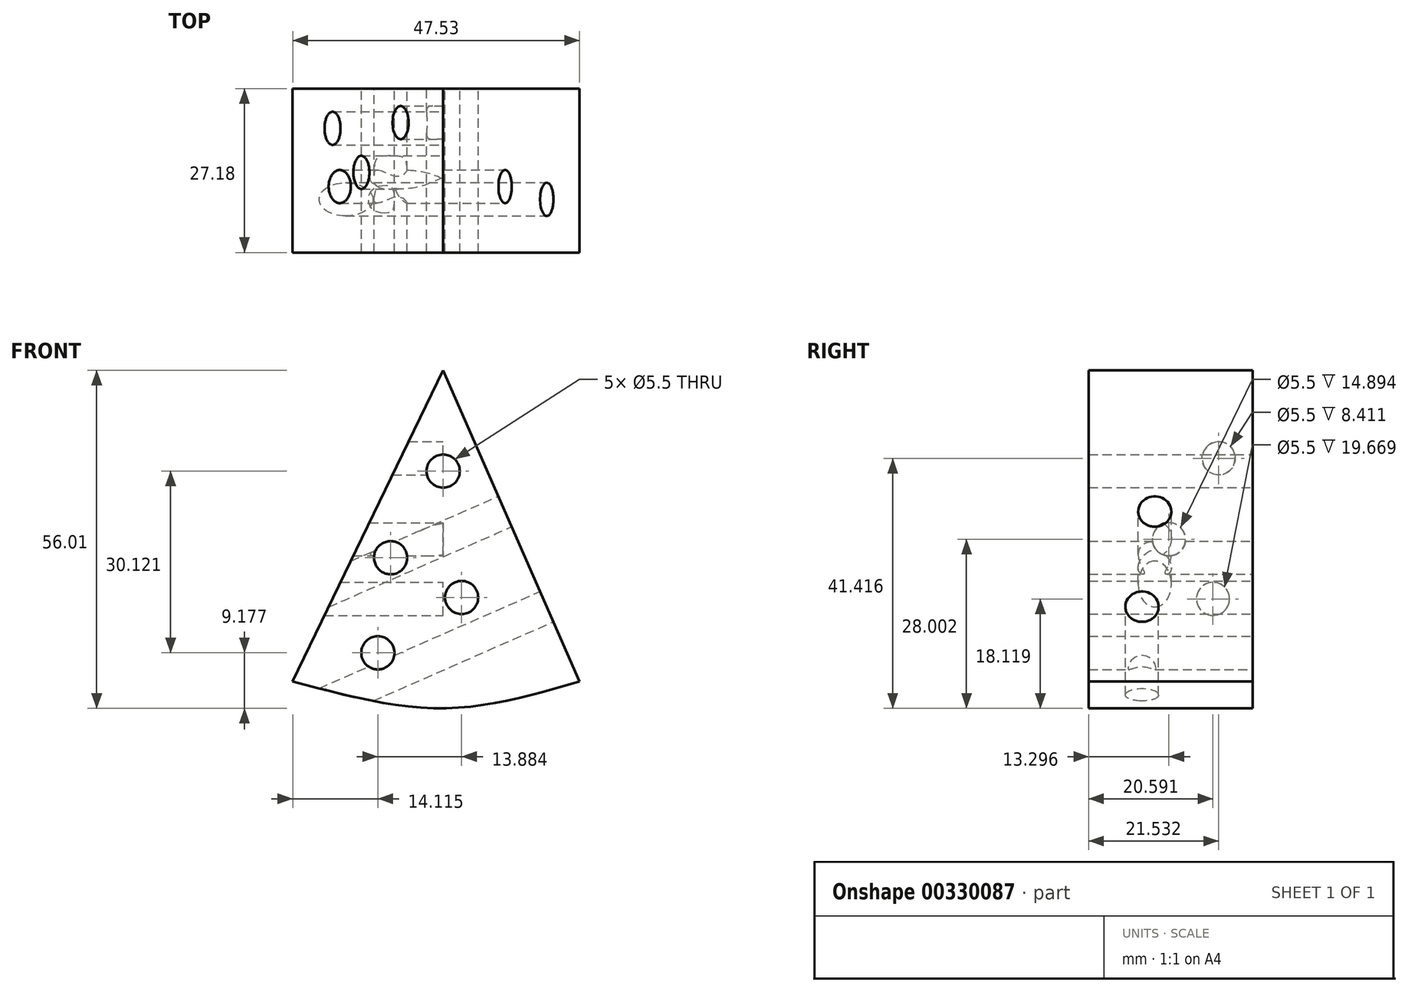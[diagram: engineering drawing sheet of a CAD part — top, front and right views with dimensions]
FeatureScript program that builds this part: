
annotation { "Feature Type Name" : "Feature", "Feature Type Description" : "" }
export const myFeature = defineFeature(function(context is Context, id is Id, definition is map)
    precondition{}
    {
        {
            var Q0;
            Q0=qCreatedBy(makeId("Front.planeOp"),FACE);
            var sketch = newSketch(context, id + "F0", { "sketchPlane" : qUnion([Q0])});
            skLineSegment(sketch, "E0", {"start": v(0, 51.54) * mm, "end": v(-24.94, 0) * mm});
            skFitSpline(sketch, "E1", {"points": [v(-24.94, 0) * mm, v(0, -4.47) * mm, v(22.6, 0) * mm], "startDerivative": vector(49.35, -13.31) * mm, "endDerivative": vector(45.7, 13.53) * mm});
            skLineSegment(sketch, "E2", {"start": v(0, 51.54) * mm, "end": v(22.6, 0) * mm});
            skSolve(sketch);
        }
        {
            var Q0;
            Q0=makeQuery(id+"F0.imprint","IMPRINT",FACE,{"disambiguationData":[TD([[makeQuery(id+"F0.imprint","IMPRINT",EDGE,{"derivedFrom":sQuery(id+"F0.wireOp",EDGE,"E0")}),1.0]])]});
            extrude(context, id + "F1", {"entities" : qUnion([Q0]), "depth" : 27.18 * mm});
        }
        {
            var Q0;
            Q0=qCreatedBy(makeId("Front.planeOp"),FACE);
            var sketch = newSketch(context, id + "F2", { "sketchPlane" : qUnion([Q0])});
            skCircle(sketch, "E3", {"center": v(-10.82, 4.7) * mm, "radius": 3.5 * mm});
            skCircle(sketch, "E4", {"center": v(3.06, 13.88) * mm, "radius": 3.8 * mm});
            skCircle(sketch, "E5", {"center": v(0, 34.83) * mm, "radius": 4.1 * mm});
            skCircle(sketch, "E6", {"center": v(-8.7, 20.47) * mm, "radius": 3.83 * mm});
            skSolve(sketch);
        }
        {
            var Q0;
            Q0=sQuery(id+"F2.wireOp",VERTEX,"E5.center");
            var Q1;
            Q1=sQuery(id+"F2.wireOp",VERTEX,"E6.center");
            var Q2;
            Q2=sQuery(id+"F2.wireOp",VERTEX,"E4.center");
            var Q3;
            Q3=sQuery(id+"F2.wireOp",VERTEX,"E3.center");
            var Q4;
            Q4=makeQuery(id+"F1.opExtrude","SWEPT_BODY",BODY,{"disambiguationData":[OSD([sQuery(id+"F0.wireOp",EDGE,"E0"),sQuery(id+"F0.wireOp",EDGE,"E1"),sQuery(id+"F0.wireOp",EDGE,"E2")])]});
            hole(context, id + "F3", {"style" : HoleStyle.SIMPLE, "endStyle" : HoleEndStyle.THROUGH, "oppositeDirection" : true, "holeDiameter" : 5.5 * mm, "tappedDepth" : 12.7 * mm, "tapClearance" : 3, "startFromSketch" : true, "locations" : qUnion([Q0, Q1, Q2, Q3]), "scope" : qUnion([Q4])});
        }
        {
            var Q0;
            Q0=qCreatedBy(makeId("Right.planeOp"),FACE);
            var sketch = newSketch(context, id + "F4", { "sketchPlane" : qUnion([Q0])});
            skCircle(sketch, "E7", {"center": v(-5.65, 36.95) * mm, "radius": 2.87 * mm});
            skCircle(sketch, "E8", {"center": v(-13.88, 23.53) * mm, "radius": 2.12 * mm});
            skCircle(sketch, "E9", {"center": v(-6.59, 13.65) * mm, "radius": 2.23 * mm});
            skSolve(sketch);
        }
        {
            var Q0;
            Q0=sQuery(id+"F4.wireOp",VERTEX,"E7.center");
            var Q1;
            Q1=sQuery(id+"F4.wireOp",VERTEX,"E8.center");
            var Q2;
            Q2=sQuery(id+"F4.wireOp",VERTEX,"E9.center");
            var Q3;
            Q3=makeQuery(id+"F1.opExtrude","SWEPT_BODY",BODY,{"disambiguationData":[OSD([sQuery(id+"F0.wireOp",EDGE,"E0"),sQuery(id+"F0.wireOp",EDGE,"E1"),sQuery(id+"F0.wireOp",EDGE,"E2")])]});
            hole(context, id + "F5", {"style" : HoleStyle.SIMPLE, "endStyle" : HoleEndStyle.THROUGH, "holeDiameter" : 5.5 * mm, "tappedDepth" : 12.7 * mm, "tapClearance" : 3, "startFromSketch" : true, "locations" : qUnion([Q0, Q1, Q2]), "scope" : qUnion([Q3])});
        }
        {
            var Q0;
            Q0=makeQuery(id+"F1.opExtrude","SWEPT_FACE",FACE,{"disambiguationData":[OSD([sQuery(id+"F0.wireOp",EDGE,"E2")])]});
            var sketch = newSketch(context, id + "F6", { "sketchPlane" : qUnion([Q0])});
            skCircle(sketch, "E10", {"center": v(-16.24, 21.64) * mm, "radius": 2.5 * mm});
            skCircle(sketch, "E11", {"center": v(-18.36, 4.43) * mm, "radius": 3.1 * mm});
            skSolve(sketch);
        }
        {
            var Q0;
            Q0=sQuery(id+"F6.wireOp",VERTEX,"E11.center");
            var Q1;
            Q1=sQuery(id+"F6.wireOp",VERTEX,"E10.center");
            var Q2;
            Q2=makeQuery(id+"F1.opExtrude","SWEPT_BODY",BODY,{"disambiguationData":[OSD([sQuery(id+"F0.wireOp",EDGE,"E0"),sQuery(id+"F0.wireOp",EDGE,"E1"),sQuery(id+"F0.wireOp",EDGE,"E2")])]});
            hole(context, id + "F7", {"style" : HoleStyle.SIMPLE, "endStyle" : HoleEndStyle.THROUGH, "holeDiameter" : 5.5 * mm, "tappedDepth" : 12.7 * mm, "tapClearance" : 3, "startFromSketch" : true, "locations" : qUnion([Q0, Q1]), "scope" : qUnion([Q2])});
        }
    });
